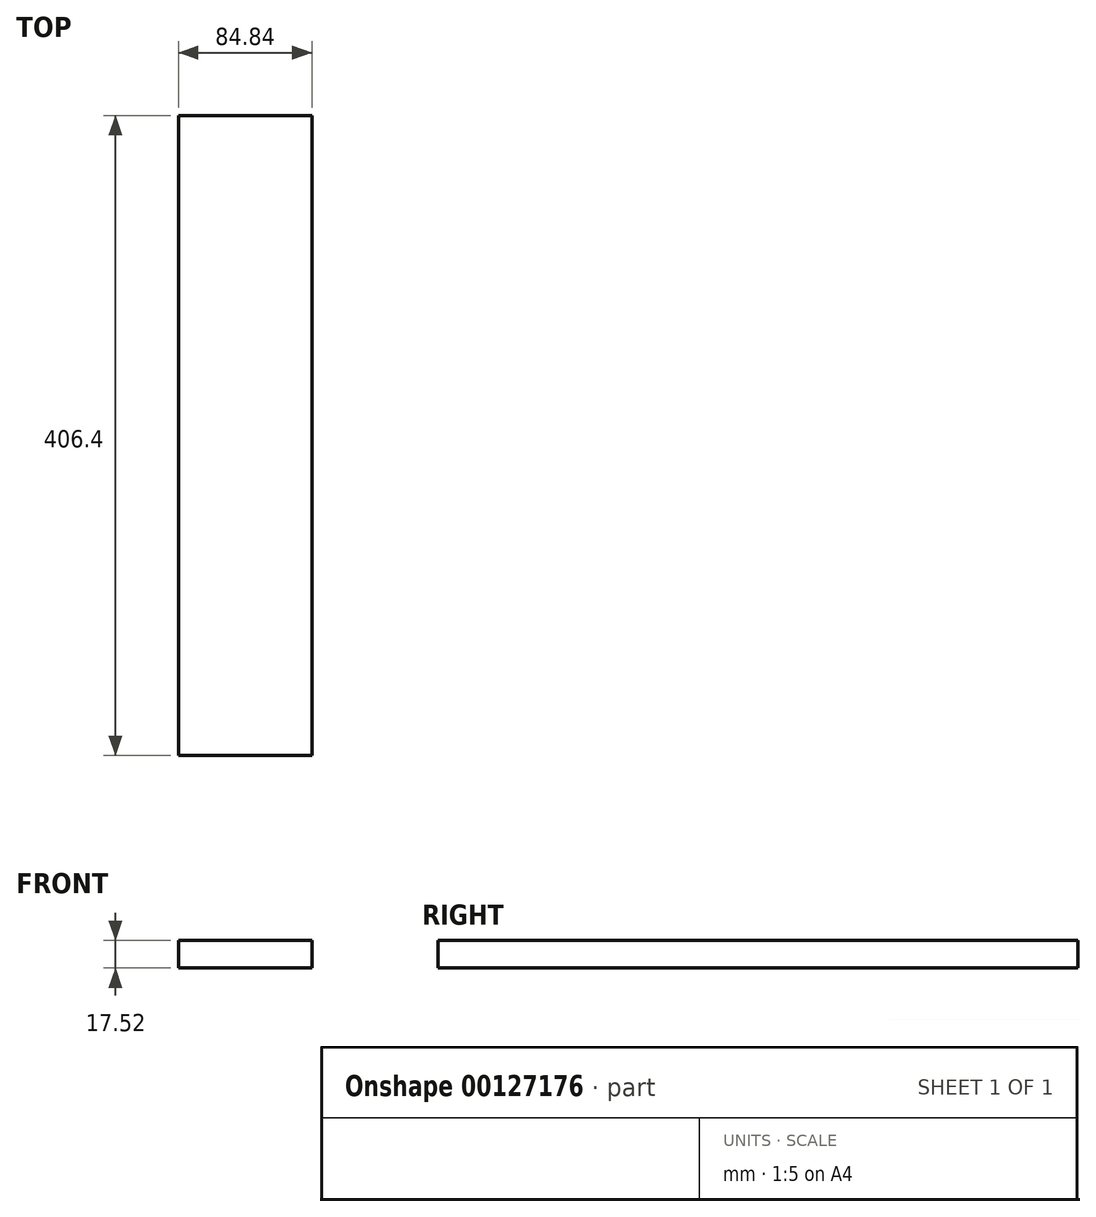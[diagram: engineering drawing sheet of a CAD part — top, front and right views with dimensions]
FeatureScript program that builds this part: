
annotation { "Feature Type Name" : "Feature", "Feature Type Description" : "" }
export const myFeature = defineFeature(function(context is Context, id is Id, definition is map)
    precondition{}
    {
        {
            var Q0;
            Q0=qCreatedBy(makeId("Front.planeOp"),FACE);
            var sketch = newSketch(context, id + "F0", { "sketchPlane" : qUnion([Q0])});
            skLineSegment(sketch, "E0.bottom", {"start": v(42.42, -8.76) * mm, "end": v(-42.42, -8.76) * mm});
            skLineSegment(sketch, "E0.top", {"start": v(42.42, 8.76) * mm, "end": v(-42.42, 8.76) * mm});
            skLineSegment(sketch, "E0.left", {"start": v(42.42, -8.76) * mm, "end": v(42.42, 8.76) * mm});
            skLineSegment(sketch, "E0.right", {"start": v(-42.42, -8.76) * mm, "end": v(-42.42, 8.76) * mm});
            skPoint(sketch, "E0.middle", {"position": v(0, 0) * mm});
            skSolve(sketch);
        }
        {
            var Q0;
            Q0=qSketchRegion(id+"F0",true);
            extrude(context, id + "F1", {"entities" : qUnion([Q0]), "depth" : 406.4 * mm, "offsetDistance" : 25.4 * mm});
        }
    });
